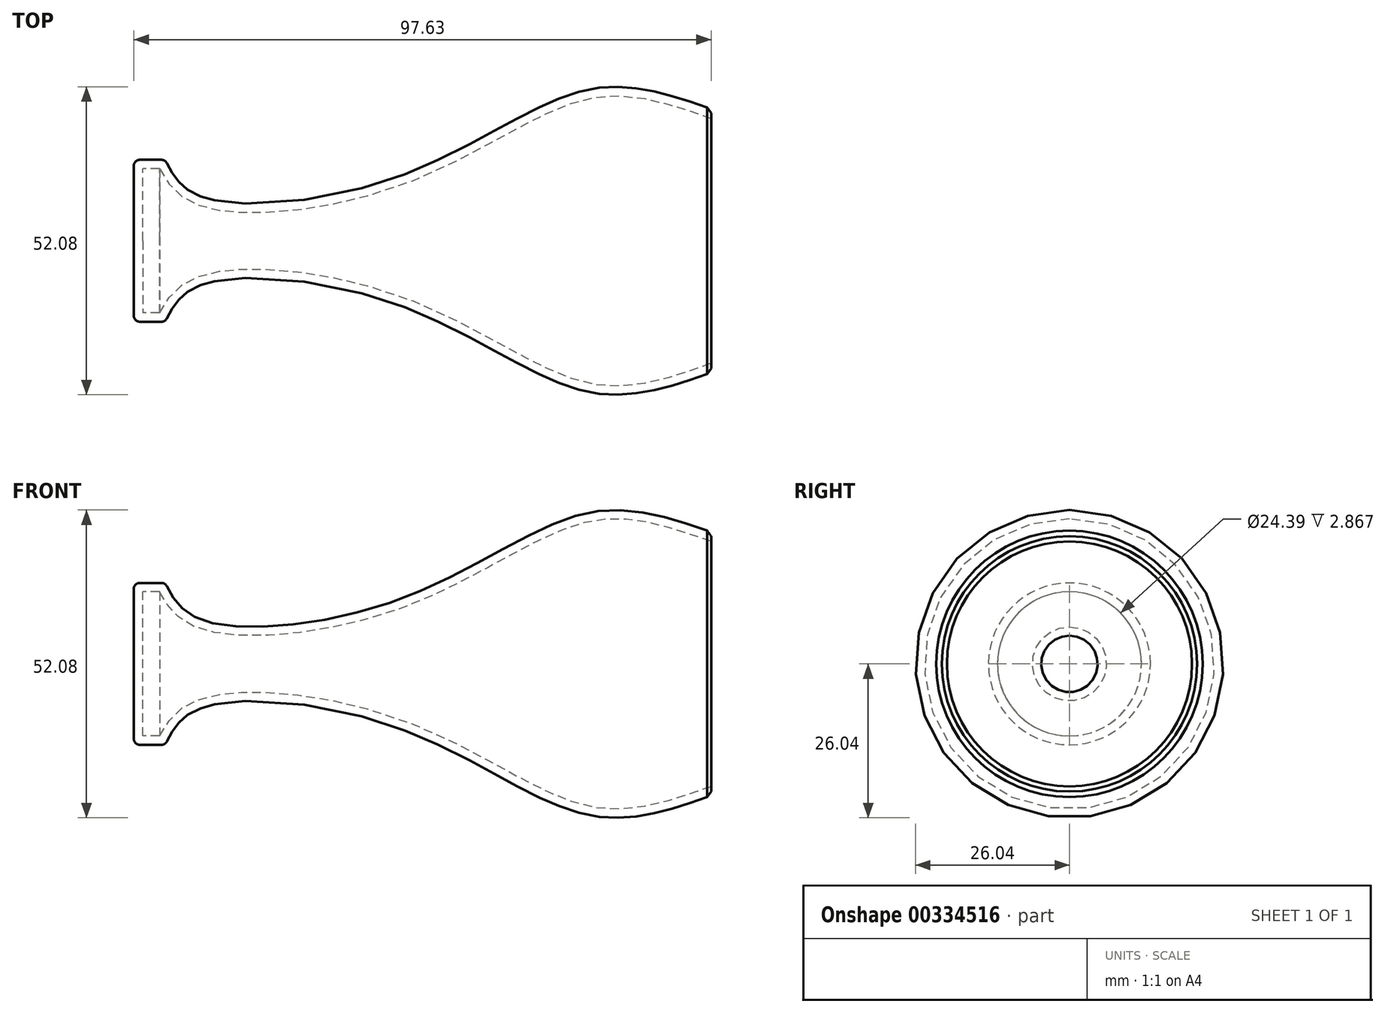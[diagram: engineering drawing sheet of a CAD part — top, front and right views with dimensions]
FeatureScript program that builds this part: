
annotation { "Feature Type Name" : "Feature", "Feature Type Description" : "" }
export const myFeature = defineFeature(function(context is Context, id is Id, definition is map)
    precondition{}
    {
        {
            var Q0;
            Q0=qCreatedBy(makeId("Top.planeOp"),FACE);
            var sketch = newSketch(context, id + "F0", { "sketchPlane" : qUnion([Q0])});
            skLineSegment(sketch, "E0", {"start": v(50.58, 0) * mm, "end": v(50.58, -22.3) * mm});
            skFitSpline(sketch, "E1", {"points": [v(50.58, -22.3) * mm, v(30.03, -25.63) * mm, v(-1.47, -11.15) * mm, v(-36.1, -7.63) * mm, v(-41.77, -13.7) * mm], "startDerivative": vector(-85.02, -29.7) * mm, "endDerivative": vector(-24.07, -47.27) * mm});
            skLineSegment(sketch, "E2", {"start": v(-41.77, -13.7) * mm, "end": v(-47.05, -13.7) * mm});
            skLineSegment(sketch, "E3", {"start": v(-47.05, -13.7) * mm, "end": v(-47.05, 0) * mm});
            skLineSegment(sketch, "E4", {"start": v(-47.05, 0) * mm, "end": v(50.58, 0) * mm});
            skSolve(sketch);
        }
        {
            var Q0;
            Q0=makeQuery(id+"F0.imprint","IMPRINT",FACE,{"disambiguationData":[TD([[makeQuery(id+"F0.imprint","IMPRINT",EDGE,{"derivedFrom":sQuery(id+"F0.wireOp",EDGE,"E0")}),-1.0]])]});
            var Q1;
            Q1=sQuery(id+"F0.wireOp",EDGE,"E4");
            revolve(context, id + "F1", {"entities" : qUnion([Q0]), "axis" : qUnion([Q1]), "revolveType" : RevolveType.ONE_DIRECTION, "angle" : 360 * degree});
        }
        {
            var Q0;
            Q0=makeQuery(id+"F1.opRevolve","SWEPT_FACE",FACE,{"disambiguationData":[OSD([sQuery(id+"F0.wireOp",EDGE,"E0")])]});
            shell(context, id + "F2", {"entities" : qUnion([Q0]), "thickness" : 1.5 * mm});
        }
        {
            var Q0;
            Q0=makeQuery(id+"F1.opRevolve","SWEPT_EDGE",EDGE,{"disambiguationData":[OSD([sQuery(id+"F0.wireOp",EDGE,"E1"),sQuery(id+"F0.wireOp",EDGE,"E2")])]});
            fillet(context, id + "F3", {"entities" : qUnion([Q0]), "radius" : 1 * mm, "tangentPropagation" : true, "allowEdgeOverflow" : false});
        }
        {
            var Q0;
            Q0=makeQuery(id+"F1.opRevolve","SWEPT_EDGE",EDGE,{"disambiguationData":[OSD([sQuery(id+"F0.wireOp",EDGE,"E2"),sQuery(id+"F0.wireOp",EDGE,"E3")])]});
            fillet(context, id + "F4", {"entities" : qUnion([Q0]), "radius" : 1 * mm, "tangentPropagation" : true, "allowEdgeOverflow" : false});
        }
        {
            var Q0;
            Q0=makeQuery(id+"F1.opRevolve","SWEPT_EDGE",EDGE,{"disambiguationData":[OSD([sQuery(id+"F0.wireOp",EDGE,"E0"),sQuery(id+"F0.wireOp",EDGE,"E1")])]});
            chamfer(context, id + "F5", {"entities" : qUnion([Q0]), "width" : 1 * mm, "tangentPropagation" : true});
        }
    });
